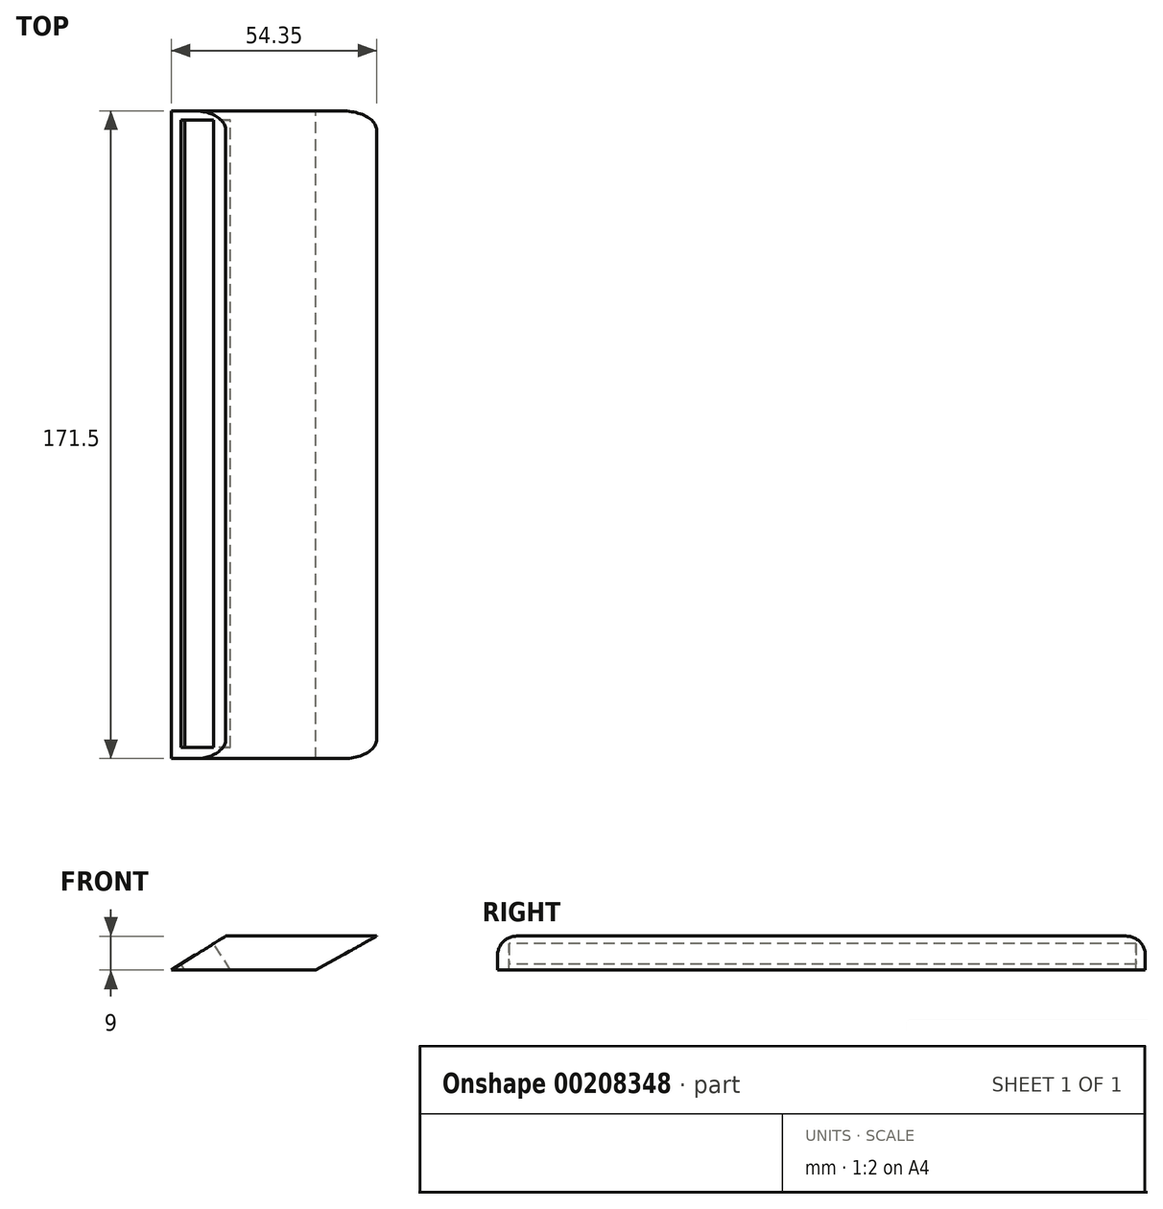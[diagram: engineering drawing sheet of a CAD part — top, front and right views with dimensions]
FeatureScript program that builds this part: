
annotation { "Feature Type Name" : "Feature", "Feature Type Description" : "" }
export const myFeature = defineFeature(function(context is Context, id is Id, definition is map)
    precondition{}
    {
        {
            var Q0;
            Q0=qCreatedBy(makeId("Front.planeOp"),FACE);
            var sketch = newSketch(context, id + "F0", { "sketchPlane" : qUnion([Q0])});
            skLineSegment(sketch, "E0", {"start": v(-22.66, 0) * mm, "end": v(-8.29, 9) * mm});
            skLineSegment(sketch, "E1", {"start": v(-8.29, 9) * mm, "end": v(31.7, 9) * mm});
            skLineSegment(sketch, "E2", {"start": v(31.7, 9) * mm, "end": v(15.59, 0) * mm});
            skLineSegment(sketch, "E3", {"start": v(15.59, 0) * mm, "end": v(-22.66, 0) * mm});
            skSolve(sketch);
        }
        {
            var Q0;
            Q0 = qSketchRegion(id + "F0", true);
            extrude(context, id + "F1", {"entities" : qUnion([Q0]), "depth" : 89.5 * mm});
        }
        {
            var Q0;
            Q0=makeQuery(id+"F1.opExtrude","CAP_FACE",FACE,{"disambiguationData":[OSD([sQuery(id+"F0.wireOp",EDGE,"E0"),sQuery(id+"F0.wireOp",EDGE,"E1"),sQuery(id+"F0.wireOp",EDGE,"E2"),sQuery(id+"F0.wireOp",EDGE,"E3")])],"isStart":true});
            extrude(context, id + "F4", {"entities" : qUnion([Q0]), "operationType" : NewBodyOperationType.ADD, "depth" : 82 * mm});
        }
        {
            var Q0;
            {var subQ0=sQuery(id+"F0.wireOp",EDGE,"E0");Q0=makeQuery(id+"F4.boolean.opBoolean","MERGE",FACE,{"derivedFrom":[makeQuery(id+"F1.opExtrude","SWEPT_FACE",FACE,{"disambiguationData":[OSD([subQ0])]}),makeQuery(id+"F4.opExtrude","SWEPT_FACE",FACE,{"disambiguationData":[OSD([subQ0])]})]});}
            var sketch = newSketch(context, id + "F2", { "sketchPlane" : qUnion([Q0])});
            skLineSegment(sketch, "E4.bottom", {"start": v(-5.96, 79.53) * mm, "end": v(-16.24, 79.53) * mm});
            skLineSegment(sketch, "E4.top", {"start": v(-5.96, 36.19) * mm, "end": v(-16.24, 36.19) * mm});
            skLineSegment(sketch, "E4.left", {"start": v(-5.96, 79.53) * mm, "end": v(-5.96, 36.19) * mm});
            skLineSegment(sketch, "E4.right", {"start": v(-16.24, 79.53) * mm, "end": v(-16.24, 36.19) * mm});
            skLineSegment(sketch, "E5.top", {"start": v(-5.96, 0) * mm, "end": v(-16.24, 0) * mm});
            skLineSegment(sketch, "E5.left", {"start": v(-5.96, 36.19) * mm, "end": v(-5.96, 0) * mm});
            skLineSegment(sketch, "E5.right", {"start": v(-16.24, 36.19) * mm, "end": v(-16.24, 0) * mm});
            skLineSegment(sketch, "E6.top", {"start": v(-5.96, -36.77) * mm, "end": v(-16.24, -36.77) * mm});
            skLineSegment(sketch, "E6.left", {"start": v(-5.96, 0) * mm, "end": v(-5.96, -36.77) * mm});
            skLineSegment(sketch, "E6.right", {"start": v(-16.24, 0) * mm, "end": v(-16.24, -36.77) * mm});
            skLineSegment(sketch, "E7.top", {"start": v(-5.96, -86.51) * mm, "end": v(-16.24, -86.51) * mm});
            skLineSegment(sketch, "E7.left", {"start": v(-5.96, -36.77) * mm, "end": v(-5.96, -86.51) * mm});
            skLineSegment(sketch, "E7.right", {"start": v(-16.24, -36.77) * mm, "end": v(-16.24, -86.51) * mm});
            skSolve(sketch);
        }
        {
            var Q0;
            Q0 = qSketchRegion(id + "F2", true);
            extrude(context, id + "F5", {"entities" : qUnion([Q0]), "operationType" : NewBodyOperationType.REMOVE, "oppositeDirection" : true, "depth" : 25.4 * mm});
        }
        {
            var Q0;
            Q0=makeQuery(id+"F1.opExtrude","CAP_EDGE",EDGE,{"disambiguationData":[OSD([sQuery(id+"F0.wireOp",EDGE,"E1")])],"isStart":false});
            fillet(context, id + "F3", {"entities" : qUnion([Q0]), "radius" : 5.08 * mm, "tangentPropagation" : true, "allowEdgeOverflow" : false});
        }
        {
            var Q0;
            Q0=makeQuery(id+"F4.opExtrude","CAP_EDGE",EDGE,{"disambiguationData":[OSD([sQuery(id+"F0.wireOp",EDGE,"E1")])],"isStart":false});
            fillet(context, id + "F6", {"entities" : qUnion([Q0]), "radius" : 5.08 * mm, "tangentPropagation" : true, "allowEdgeOverflow" : false});
        }
    });
